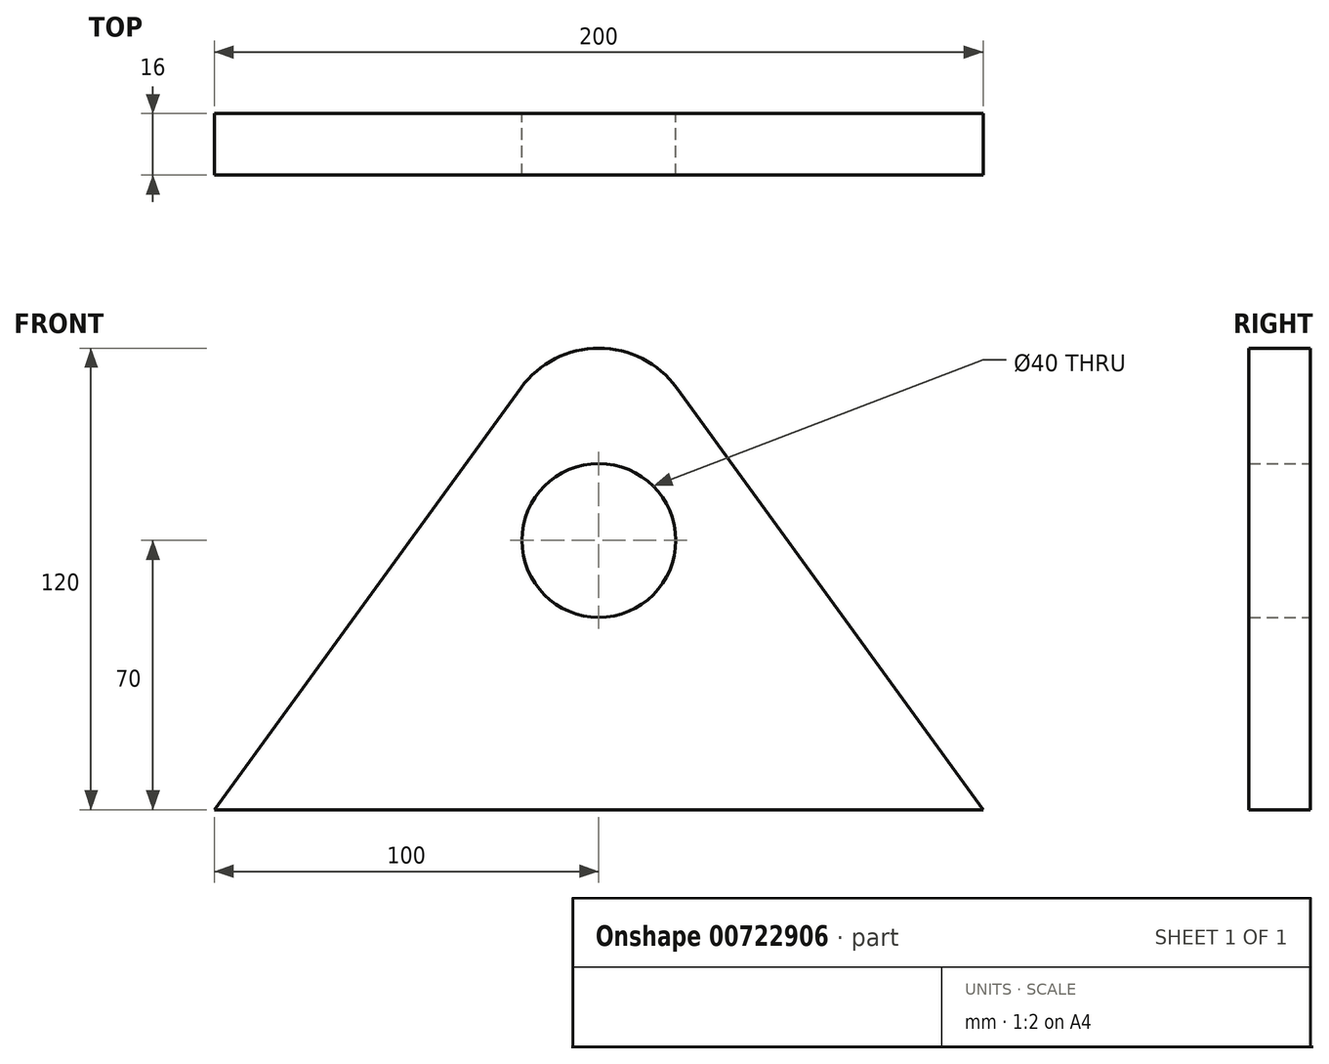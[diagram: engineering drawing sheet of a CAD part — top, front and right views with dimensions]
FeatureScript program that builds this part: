
annotation { "Feature Type Name" : "Feature", "Feature Type Description" : "" }
export const myFeature = defineFeature(function(context is Context, id is Id, definition is map)
    precondition{}
    {
        {
            var Q0;
            Q0=qCreatedBy(makeId("Front.planeOp"),FACE);
            var sketch = newSketch(context, id + "F0", { "sketchPlane" : qUnion([Q0])});
            skCircle(sketch, "E0", {"center": v(0, 0) * mm, "radius": 25 * mm});
            skLineSegment(sketch, "E1", {"start": v(0, -95) * mm, "end": v(100, -95) * mm});
            skLineSegment(sketch, "E2", {"start": v(0, -95) * mm, "end": v(-100, -95) * mm});
            skLineSegment(sketch, "E3", {"start": v(-100, -95) * mm, "end": v(-20.22, 14.7) * mm});
            skLineSegment(sketch, "E4", {"start": v(100, -95) * mm, "end": v(20.22, 14.7) * mm});
            skLineSegment(sketch, "E5", {"start": v(0, 0) * mm, "end": v(0, 25) * mm});
            skCircle(sketch, "E6", {"center": v(0, -25) * mm, "radius": 20 * mm});
            skLineSegment(sketch, "E7", {"start": v(0, -25) * mm, "end": v(0, -5) * mm});
            skSolve(sketch);
        }
        {
            var Q0;
            Q0 = qSketchRegion(id + "F0", true);
            extrude(context, id + "F1", {"entities" : qUnion([Q0]), "depth" : 16 * mm, "offsetDistance" : 25 * mm});
        }
    });
